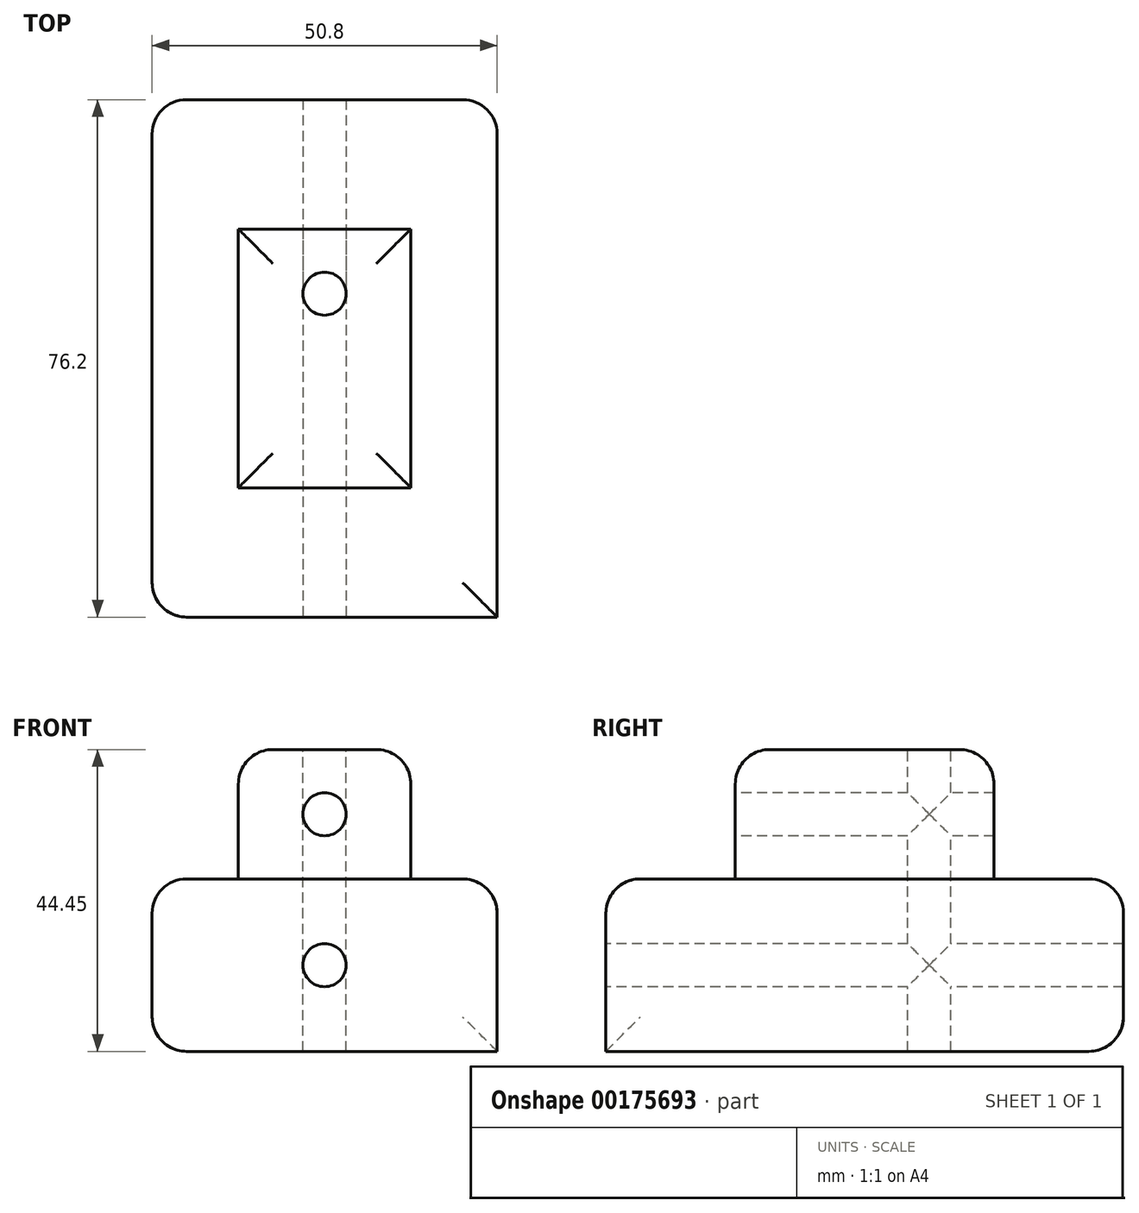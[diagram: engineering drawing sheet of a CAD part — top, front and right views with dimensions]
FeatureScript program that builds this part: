
annotation { "Feature Type Name" : "Feature", "Feature Type Description" : "" }
export const myFeature = defineFeature(function(context is Context, id is Id, definition is map)
    precondition{}
    {
        {
            var Q0;
            Q0=qCreatedBy(makeId("Front.planeOp"),FACE);
            var sketch = newSketch(context, id + "F0", { "sketchPlane" : qUnion([Q0])});
            skLineSegment(sketch, "E0.bottom", {"start": v(0, 0) * mm, "end": v(-50.8, 0) * mm});
            skLineSegment(sketch, "E0.top", {"start": v(0, 25.4) * mm, "end": v(-50.8, 25.4) * mm});
            skLineSegment(sketch, "E0.left", {"start": v(0, 0) * mm, "end": v(0, 25.4) * mm});
            skLineSegment(sketch, "E0.right", {"start": v(-50.8, 0) * mm, "end": v(-50.8, 25.4) * mm});
            skSolve(sketch);
        }
        {
            var Q0;
            Q0=qSketchRegion(id+"F0",true);
            extrude(context, id + "F1", {"entities" : qUnion([Q0]), "depth" : 76.2 * mm});
        }
        {
            var Q0;
            Q0=makeQuery(id+"F1.opExtrude","SWEPT_FACE",FACE,{"disambiguationData":[OSD([sQuery(id+"F0.wireOp",EDGE,"E0.top")])]});
            var sketch = newSketch(context, id + "F2", { "sketchPlane" : qUnion([Q0])});
            skLineSegment(sketch, "E1.bottom", {"start": v(-38.1, -19.05) * mm, "end": v(-12.7, -19.05) * mm});
            skLineSegment(sketch, "E1.top", {"start": v(-38.1, -57.15) * mm, "end": v(-12.7, -57.15) * mm});
            skLineSegment(sketch, "E1.left", {"start": v(-38.1, -19.05) * mm, "end": v(-38.1, -57.15) * mm});
            skLineSegment(sketch, "E1.right", {"start": v(-12.7, -19.05) * mm, "end": v(-12.7, -57.15) * mm});
            skSolve(sketch);
        }
        {
            var Q0;
            Q0=qSketchRegion(id+"F2",true);
            extrude(context, id + "F3", {"entities" : qUnion([Q0]), "operationType" : NewBodyOperationType.ADD, "depth" : 19.05 * mm});
        }
        {
            var Q0;
            Q0=makeQuery(id+"F3.opExtrude","CAP_FACE",FACE,{"disambiguationData":[OSD([sQuery(id+"F2.wireOp",EDGE,"E1.bottom"),sQuery(id+"F2.wireOp",EDGE,"E1.top"),sQuery(id+"F2.wireOp",EDGE,"E1.left"),sQuery(id+"F2.wireOp",EDGE,"E1.right")])],"isStart":false});
            var sketch = newSketch(context, id + "F4", { "sketchPlane" : qUnion([Q0])});
            skCircle(sketch, "E2", {"center": v(-25.4, -28.58) * mm, "radius": 3.18 * mm});
            skSolve(sketch);
        }
        {
            var Q0;
            Q0=makeQuery(id+"F4.imprint","IMPRINT",FACE,{"disambiguationData":[TD([[makeQuery(id+"F4.imprint","IMPRINT",EDGE,{"derivedFrom":sQuery(id+"F4.wireOp",EDGE,"E2")}),1.0]])]});
            extrude(context, id + "F5", {"entities" : qUnion([Q0]), "operationType" : NewBodyOperationType.REMOVE, "oppositeDirection" : true, "depth" : 44.45 * mm});
        }
        {
            var Q0;
            Q0=makeQuery(id+"F1.opExtrude","CAP_FACE",FACE,{"disambiguationData":[OSD([sQuery(id+"F0.wireOp",EDGE,"E0.bottom"),sQuery(id+"F0.wireOp",EDGE,"E0.top"),sQuery(id+"F0.wireOp",EDGE,"E0.left"),sQuery(id+"F0.wireOp",EDGE,"E0.right")])],"isStart":false});
            var sketch = newSketch(context, id + "F6", { "sketchPlane" : qUnion([Q0])});
            skCircle(sketch, "E3", {"center": v(-25.4, 12.7) * mm, "radius": 3.18 * mm});
            skSolve(sketch);
        }
        {
            var Q0;
            Q0=makeQuery(id+"F6.imprint","IMPRINT",FACE,{"disambiguationData":[TD([[makeQuery(id+"F6.imprint","IMPRINT",EDGE,{"derivedFrom":sQuery(id+"F6.wireOp",EDGE,"E3")}),1.0]])]});
            extrude(context, id + "F7", {"entities" : qUnion([Q0]), "operationType" : NewBodyOperationType.REMOVE, "oppositeDirection" : true, "depth" : 76.2 * mm});
        }
        {
            var Q0;
            Q0=makeQuery(id+"F3.opExtrude","SWEPT_FACE",FACE,{"disambiguationData":[OSD([sQuery(id+"F2.wireOp",EDGE,"E1.top")])]});
            var sketch = newSketch(context, id + "F8", { "sketchPlane" : qUnion([Q0])});
            skCircle(sketch, "E4", {"center": v(-25.4, 34.93) * mm, "radius": 3.18 * mm});
            skSolve(sketch);
        }
        {
            var Q0;
            Q0=qSketchRegion(id+"F8",true);
            extrude(context, id + "F9", {"entities" : qUnion([Q0]), "operationType" : NewBodyOperationType.REMOVE, "oppositeDirection" : true, "depth" : 38.1 * mm});
        }
        {
            var Q0;
            Q0=makeQuery(id+"F3.opExtrude","CAP_EDGE",EDGE,{"disambiguationData":[OSD([sQuery(id+"F2.wireOp",EDGE,"E1.left")])],"isStart":false});
            var Q1;
            Q1=makeQuery(id+"F3.opExtrude","CAP_EDGE",EDGE,{"disambiguationData":[OSD([sQuery(id+"F2.wireOp",EDGE,"E1.bottom")])],"isStart":false});
            var Q2;
            Q2=makeQuery(id+"F3.opExtrude","CAP_EDGE",EDGE,{"disambiguationData":[OSD([sQuery(id+"F2.wireOp",EDGE,"E1.right")])],"isStart":false});
            var Q3;
            Q3=makeQuery(id+"F3.opExtrude","CAP_EDGE",EDGE,{"disambiguationData":[OSD([sQuery(id+"F2.wireOp",EDGE,"E1.top")])],"isStart":false});
            var Q4;
            Q4=makeQuery(id+"F3.opExtrude","CAP_EDGE",EDGE,{"disambiguationData":[OSD([sQuery(id+"F2.wireOp",EDGE,"E1.bottom")])],"isStart":true});
            var Q5;
            Q5=makeQuery(id+"F3.opExtrude","CAP_EDGE",EDGE,{"disambiguationData":[OSD([sQuery(id+"F2.wireOp",EDGE,"E1.left")])],"isStart":true});
            var Q6;
            Q6=makeQuery(id+"F1.opExtrude","CAP_EDGE",EDGE,{"disambiguationData":[OSD([sQuery(id+"F0.wireOp",EDGE,"E0.top")])],"isStart":true});
            var Q7;
            Q7=makeQuery(id+"F1.opExtrude","CAP_EDGE",EDGE,{"disambiguationData":[OSD([sQuery(id+"F0.wireOp",EDGE,"E0.left")])],"isStart":true});
            var Q8;
            Q8=makeQuery(id+"F1.opExtrude","CAP_EDGE",EDGE,{"disambiguationData":[OSD([sQuery(id+"F0.wireOp",EDGE,"E0.bottom")])],"isStart":true});
            var Q9;
            Q9=makeQuery(id+"F1.opExtrude","CAP_EDGE",EDGE,{"disambiguationData":[OSD([sQuery(id+"F0.wireOp",EDGE,"E0.right")])],"isStart":true});
            var Q10;
            Q10=makeQuery(id+"F1.opExtrude","SWEPT_EDGE",EDGE,{"disambiguationData":[OSD([sQuery(id+"F0.wireOp",EDGE,"E0.top"),sQuery(id+"F0.wireOp",EDGE,"E0.right")])]});
            var Q11;
            Q11=makeQuery(id+"F1.opExtrude","SWEPT_EDGE",EDGE,{"disambiguationData":[OSD([sQuery(id+"F0.wireOp",EDGE,"E0.bottom"),sQuery(id+"F0.wireOp",EDGE,"E0.right")])]});
            var Q12;
            Q12=makeQuery(id+"F1.opExtrude","CAP_EDGE",EDGE,{"disambiguationData":[OSD([sQuery(id+"F0.wireOp",EDGE,"E0.right")])],"isStart":false});
            var Q13;
            Q13=makeQuery(id+"F1.opExtrude","CAP_EDGE",EDGE,{"disambiguationData":[OSD([sQuery(id+"F0.wireOp",EDGE,"E0.top")])],"isStart":false});
            var Q14;
            Q14=makeQuery(id+"F1.opExtrude","SWEPT_EDGE",EDGE,{"disambiguationData":[OSD([sQuery(id+"F0.wireOp",EDGE,"E0.top"),sQuery(id+"F0.wireOp",EDGE,"E0.left")])]});
            fillet(context, id + "F10", {"entities" : qUnion([Q0, Q1, Q2, Q3, Q4, Q5, Q6, Q7, Q8, Q9, Q10, Q11, Q12, Q13, Q14]), "radius" : 5.08 * mm, "tangentPropagation" : true, "allowEdgeOverflow" : false});
        }
    });
